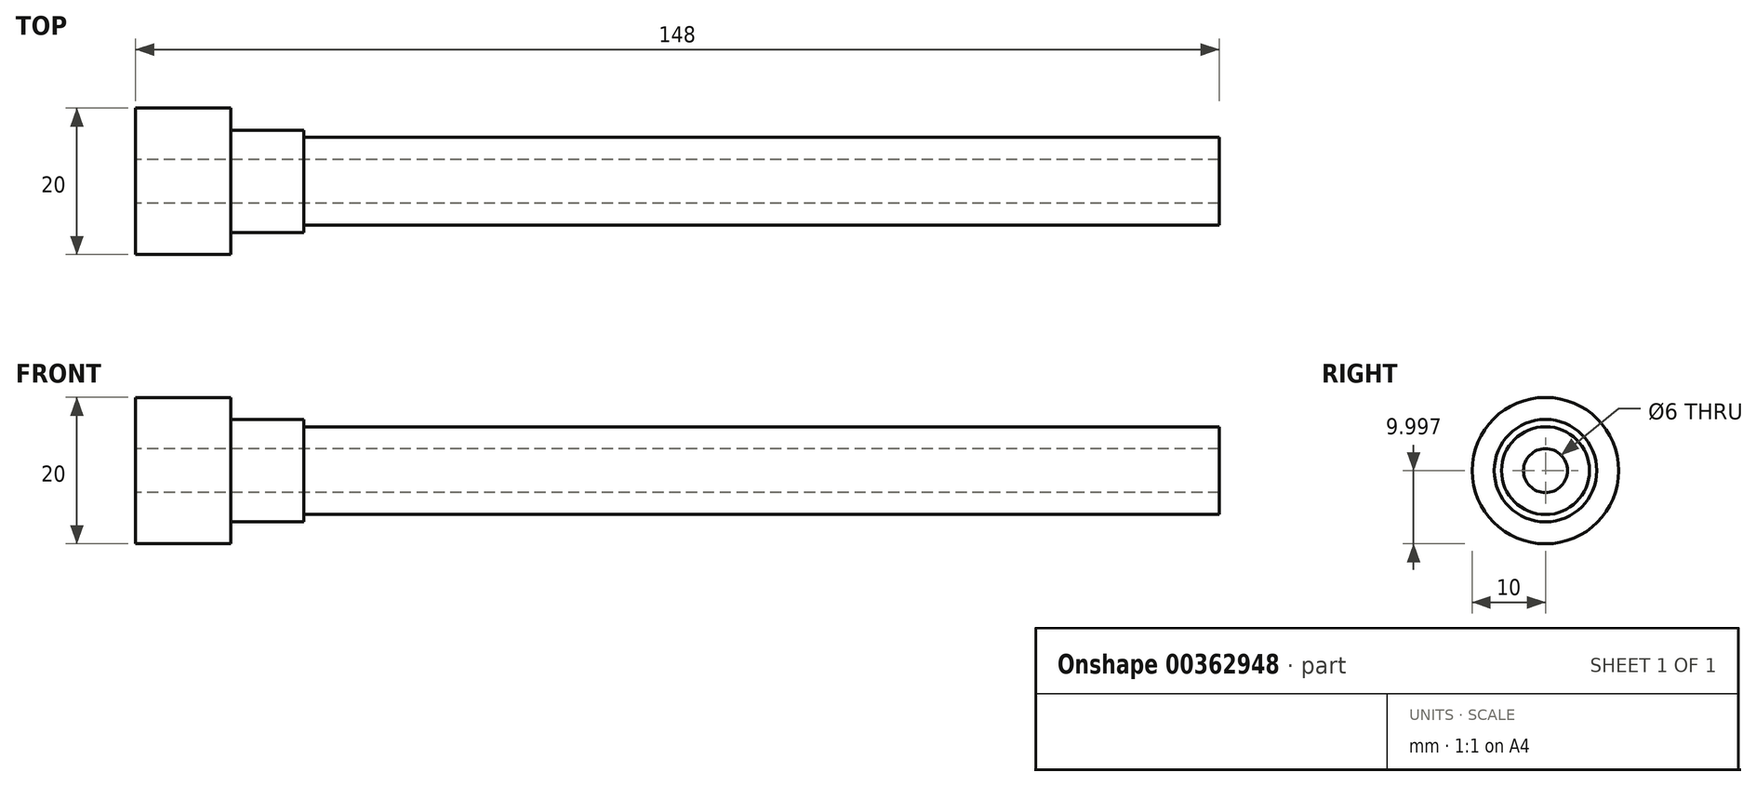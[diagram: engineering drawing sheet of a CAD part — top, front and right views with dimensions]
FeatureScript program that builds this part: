
annotation { "Feature Type Name" : "Feature", "Feature Type Description" : "" }
export const myFeature = defineFeature(function(context is Context, id is Id, definition is map)
    precondition{}
    {
        {
            var Q0;
            Q0=qCreatedBy(makeId("Front.planeOp"),FACE);
            var sketch = newSketch(context, id + "F0", { "sketchPlane" : qUnion([Q0])});
            skLineSegment(sketch, "E0.bottom", {"start": v(71.92, 10.28) * mm, "end": v(-53.08, 10.28) * mm});
            skLineSegment(sketch, "E0.top", {"start": v(71.92, 4.28) * mm, "end": v(-53.08, 4.28) * mm});
            skLineSegment(sketch, "E0.left", {"start": v(71.92, 10.28) * mm, "end": v(71.92, 4.28) * mm});
            skLineSegment(sketch, "E0.right", {"start": v(-53.08, 10.28) * mm, "end": v(-53.08, 4.28) * mm});
            skLineSegment(sketch, "E1.bottom", {"start": v(-53.08, 10.28) * mm, "end": v(-63.08, 10.28) * mm});
            skLineSegment(sketch, "E1.top", {"start": v(-53.08, 3.28) * mm, "end": v(-63.08, 3.28) * mm});
            skLineSegment(sketch, "E1.left", {"start": v(-53.08, 10.28) * mm, "end": v(-53.08, 3.28) * mm});
            skLineSegment(sketch, "E1.right", {"start": v(-63.08, 10.28) * mm, "end": v(-63.08, 3.28) * mm});
            skLineSegment(sketch, "E2.bottom", {"start": v(-63.08, 10.28) * mm, "end": v(-76.08, 10.28) * mm});
            skLineSegment(sketch, "E2.top", {"start": v(-63.08, 0.28) * mm, "end": v(-76.08, 0.28) * mm});
            skLineSegment(sketch, "E2.left", {"start": v(-63.08, 10.28) * mm, "end": v(-63.08, 0.28) * mm});
            skLineSegment(sketch, "E2.right", {"start": v(-76.08, 10.28) * mm, "end": v(-76.08, 0.28) * mm});
            skSolve(sketch);
        }
        {
            var Q0;
            {var subQ0=sQuery(id+"F0.wireOp",EDGE,"E0.bottom");Q0=makeQuery(id+"F0.imprint","IMPRINT",FACE,{"disambiguationData":[TD([[makeQuery(id+"F0.imprint","IMPRINT",EDGE,{"derivedFrom":subQ0}),1.0]])]});}
            var Q1;
            {var subQ3=sQuery(id+"F0.wireOp",EDGE,"E1.bottom");Q1=makeQuery(id+"F0.imprint","IMPRINT",FACE,{"disambiguationData":[TD([[makeQuery(id+"F0.imprint","IMPRINT",EDGE,{"derivedFrom":subQ3}),1.0]])]});}
            var Q2;
            {var subQ3=sQuery(id+"F0.wireOp",EDGE,"E2.bottom");Q2=makeQuery(id+"F0.imprint","IMPRINT",FACE,{"disambiguationData":[TD([[makeQuery(id+"F0.imprint","IMPRINT",EDGE,{"derivedFrom":subQ3}),1.0]])]});}
            var Q3;
            Q3=sQuery(id+"F0.wireOp",EDGE,"E0.bottom");
            revolve(context, id + "F1", {"entities" : qUnion([Q0, Q1, Q2]), "axis" : qUnion([Q3]), "revolveType" : RevolveType.FULL});
        }
        {
            var Q0;
            Q0=makeQuery(id+"F1.opRevolve","SWEPT_FACE",FACE,{"disambiguationData":[OSD([sQuery(id+"F0.wireOp",EDGE,"E2.right")])]});
            var sketch = newSketch(context, id + "F2", { "sketchPlane" : qUnion([Q0])});
            skCircle(sketch, "E3", {"center": v(0, 10.28) * mm, "radius": 3.56 * mm});
            skSolve(sketch);
        }
        {
            var Q0;
            Q0=sQuery(id+"F2.wireOp",VERTEX,"E3.center");
            var Q1;
            Q1=makeQuery(id+"F1.opRevolve","SWEPT_BODY",BODY,{"disambiguationData":[OSD([sQuery(id+"F0.wireOp",EDGE,"E0.bottom"),sQuery(id+"F0.wireOp",EDGE,"E0.top"),sQuery(id+"F0.wireOp",EDGE,"E0.left"),sQuery(id+"F0.wireOp",EDGE,"E1.bottom"),sQuery(id+"F0.wireOp",EDGE,"E1.top"),sQuery(id+"F0.wireOp",EDGE,"E1.left"),sQuery(id+"F0.wireOp",EDGE,"E2.bottom"),sQuery(id+"F0.wireOp",EDGE,"E2.top"),sQuery(id+"F0.wireOp",EDGE,"E2.left"),sQuery(id+"F0.wireOp",EDGE,"E2.right")])]});
            hole(context, id + "F3", {"style" : HoleStyle.SIMPLE, "endStyle" : HoleEndStyle.THROUGH, "holeDiameter" : 6 * mm, "isTappedThrough" : true, "tappedDepth" : 12 * mm, "tapClearance" : 3, "startFromSketch" : true, "locations" : qUnion([Q0]), "scope" : qUnion([Q1])});
        }
    });
